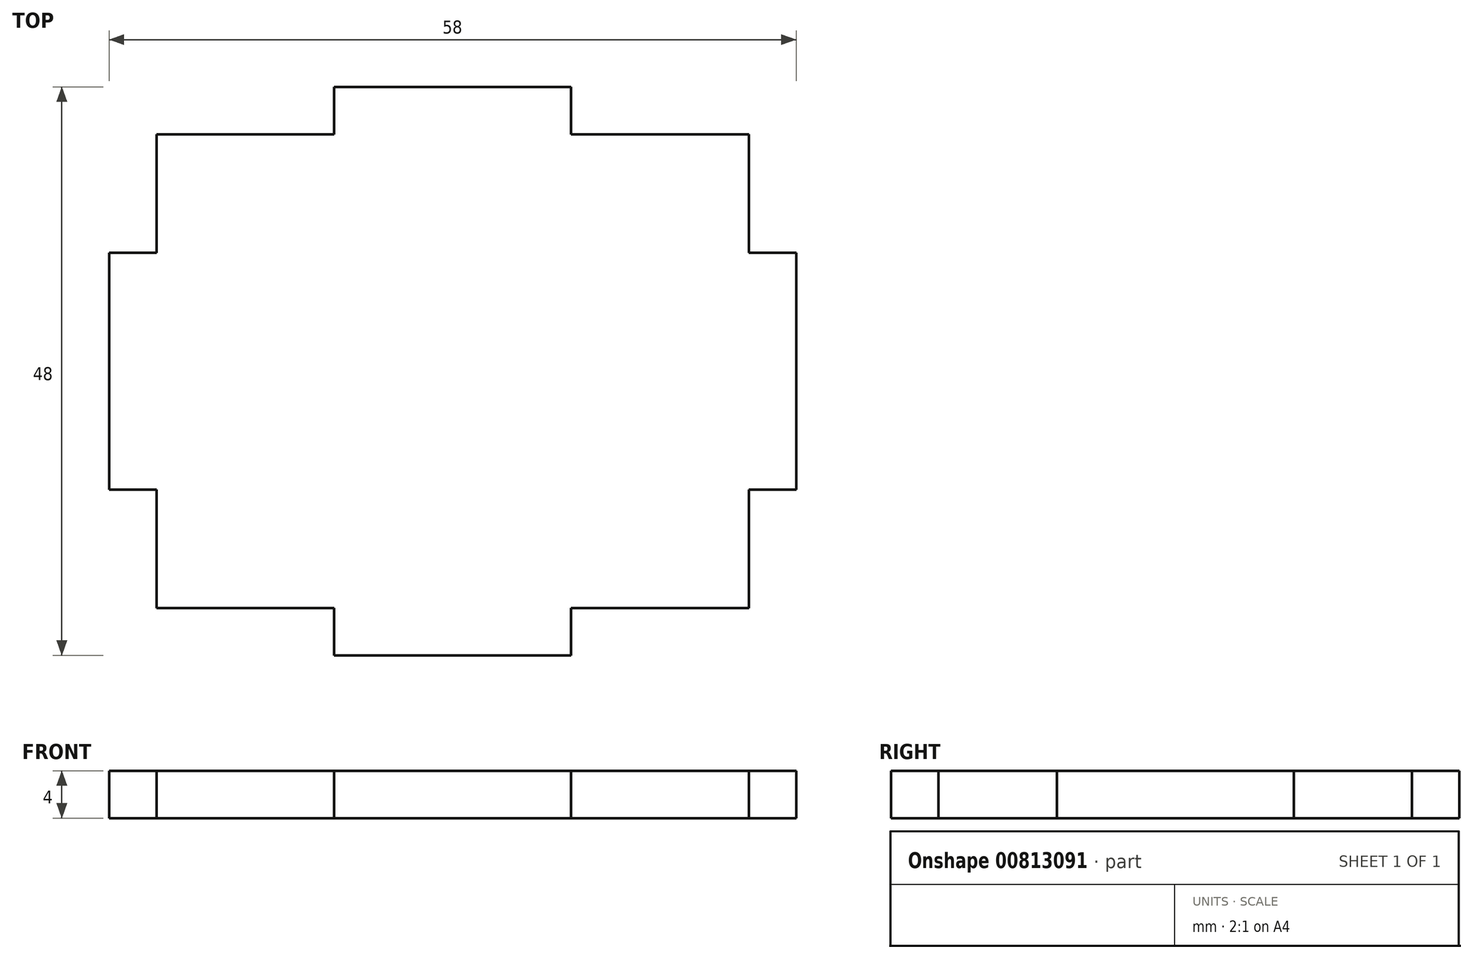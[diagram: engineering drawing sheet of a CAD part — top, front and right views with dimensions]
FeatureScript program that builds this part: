
annotation { "Feature Type Name" : "Feature", "Feature Type Description" : "" }
export const myFeature = defineFeature(function(context is Context, id is Id, definition is map)
    precondition{}
    {
        {
            var Q0;
            Q0=qCreatedBy(makeId("Top.planeOp"),FACE);
            var sketch = newSketch(context, id + "F0", { "sketchPlane" : qUnion([Q0])});
            skLineSegment(sketch, "E0.bottom", {"start": v(-25, 20) * mm, "end": v(-10, 20) * mm});
            skLineSegment(sketch, "E0.top", {"start": v(-25, -20) * mm, "end": v(-10, -20) * mm});
            skLineSegment(sketch, "E0.left", {"start": v(-25, 20) * mm, "end": v(-25, 10) * mm});
            skLineSegment(sketch, "E0.right", {"start": v(25, 20) * mm, "end": v(25, 10) * mm});
            skPoint(sketch, "E0.middle", {"position": v(0, 0) * mm});
            skLineSegment(sketch, "E1.bottom", {"start": v(-29, 10) * mm, "end": v(-25, 10) * mm});
            skLineSegment(sketch, "E1.top", {"start": v(-29, -10) * mm, "end": v(-25, -10) * mm});
            skLineSegment(sketch, "E1.left", {"start": v(-29, 10) * mm, "end": v(-29, -10) * mm});
            skLineSegment(sketch, "E1.right", {"start": v(29, 10) * mm, "end": v(29, -10) * mm});
            skLineSegment(sketch, "E2.bottom", {"start": v(-10, 24) * mm, "end": v(10, 24) * mm});
            skLineSegment(sketch, "E2.top", {"start": v(-10, -24) * mm, "end": v(10, -24) * mm});
            skLineSegment(sketch, "E2.left", {"start": v(-10, 24) * mm, "end": v(-10, 20) * mm});
            skLineSegment(sketch, "E2.right", {"start": v(10, 24) * mm, "end": v(10, 20) * mm});
            skLineSegment(sketch, "E3.trimOffspring", {"start": v(-10, -20) * mm, "end": v(-10, -24) * mm});
            skLineSegment(sketch, "E4.trimOffspring", {"start": v(25, 10) * mm, "end": v(29, 10) * mm});
            skLineSegment(sketch, "E5.trimOffspring", {"start": v(10, 20) * mm, "end": v(25, 20) * mm});
            skLineSegment(sketch, "E6.trimOffspring", {"start": v(-25, -10) * mm, "end": v(-25, -20) * mm});
            skLineSegment(sketch, "E7.trimOffspring", {"start": v(25, -10) * mm, "end": v(29, -10) * mm});
            skLineSegment(sketch, "E8.trimOffspring", {"start": v(10, -20) * mm, "end": v(10, -24) * mm});
            skLineSegment(sketch, "E9.trimOffspring", {"start": v(10, -20) * mm, "end": v(25, -20) * mm});
            skLineSegment(sketch, "E10.trimOffspring", {"start": v(25, -10) * mm, "end": v(25, -20) * mm});
            skSolve(sketch);
        }
        {
            var Q0;
            Q0=makeQuery(id+"F0.imprint","IMPRINT",FACE,{"disambiguationData":[TD([[makeQuery(id+"F0.imprint","IMPRINT",EDGE,{"derivedFrom":sQuery(id+"F0.wireOp",EDGE,"E0.bottom")}),-1.0]])]});
            extrude(context, id + "F1", {"entities" : qUnion([Q0]), "depth" : 4 * mm, "offsetDistance" : 25 * mm});
        }
    });
